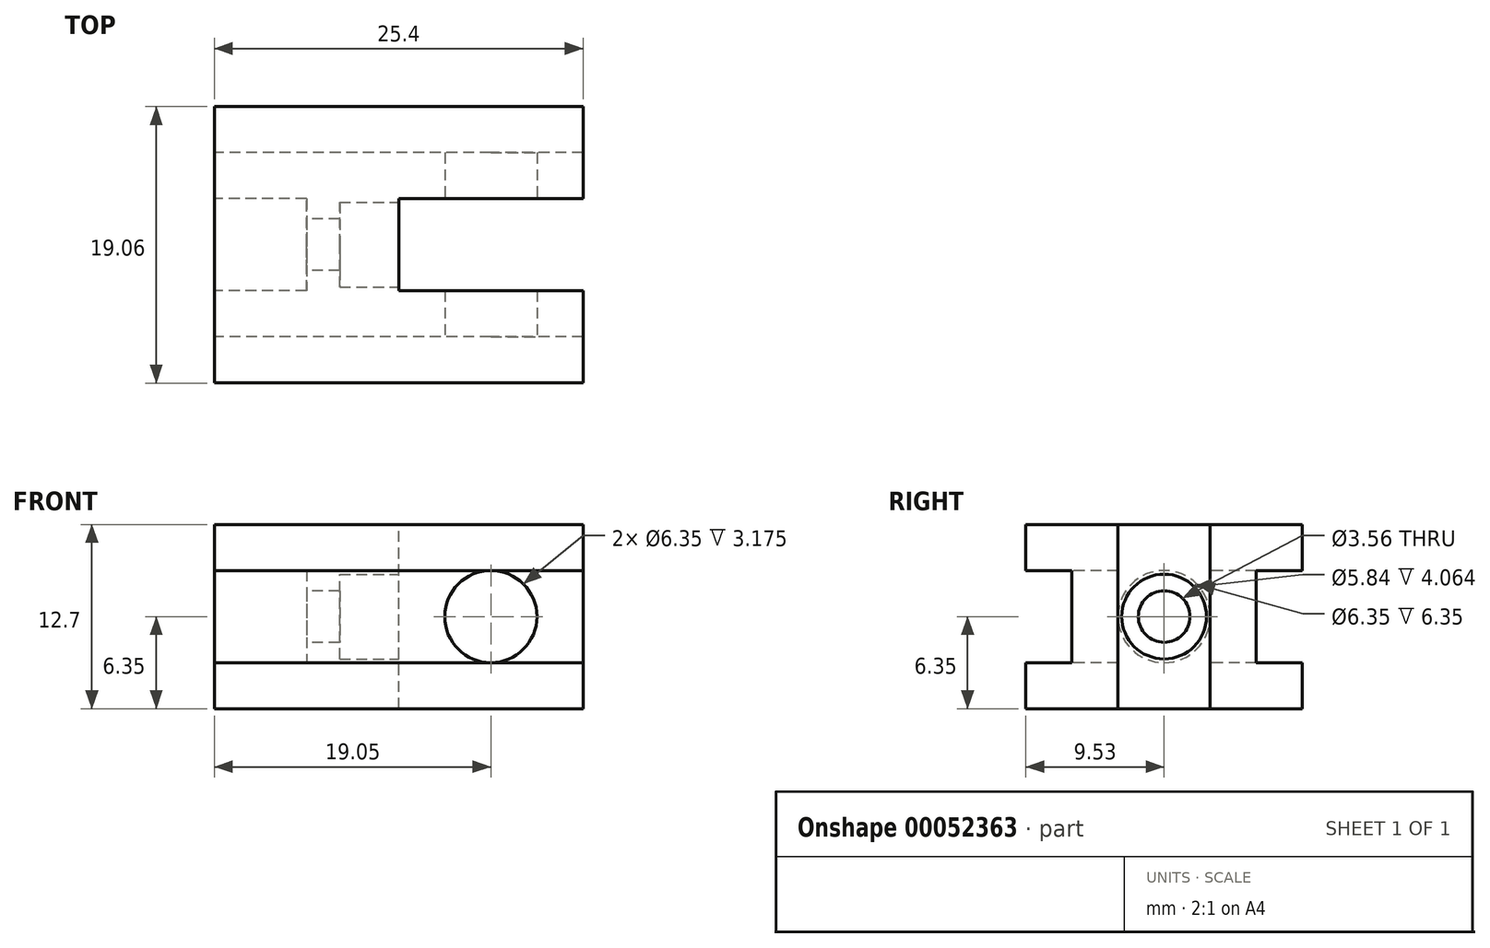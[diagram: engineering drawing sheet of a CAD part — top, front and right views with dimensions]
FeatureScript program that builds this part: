
annotation { "Feature Type Name" : "Feature", "Feature Type Description" : "" }
export const myFeature = defineFeature(function(context is Context, id is Id, definition is map)
    precondition{}
    {
        {
            var Q0;
            Q0=qCreatedBy(makeId("Right.planeOp"),FACE);
            var sketch = newSketch(context, id + "F0", { "sketchPlane" : qUnion([Q0])});
            skLineSegment(sketch, "E0", {"start": v(-6.35, -3.17) * mm, "end": v(-6.35, 3.17) * mm});
            skLineSegment(sketch, "E1", {"start": v(-6.35, 3.17) * mm, "end": v(-9.53, 3.17) * mm});
            skLineSegment(sketch, "E2", {"start": v(-9.52, 3.17) * mm, "end": v(-9.52, 6.35) * mm});
            skLineSegment(sketch, "E3", {"start": v(-9.52, 6.35) * mm, "end": v(9.52, 6.35) * mm});
            skLineSegment(sketch, "E4", {"start": v(9.53, 6.35) * mm, "end": v(9.53, 3.17) * mm});
            skLineSegment(sketch, "E5", {"start": v(9.53, 3.17) * mm, "end": v(6.35, 3.17) * mm});
            skLineSegment(sketch, "E6", {"start": v(6.35, 3.17) * mm, "end": v(6.35, -3.17) * mm});
            skLineSegment(sketch, "E7", {"start": v(6.35, -3.17) * mm, "end": v(9.53, -3.17) * mm});
            skLineSegment(sketch, "E8", {"start": v(9.52, -3.17) * mm, "end": v(9.52, -6.35) * mm});
            skLineSegment(sketch, "E9", {"start": v(9.53, -6.35) * mm, "end": v(-9.53, -6.35) * mm});
            skLineSegment(sketch, "E10", {"start": v(-9.53, -6.35) * mm, "end": v(-9.53, -3.17) * mm});
            skLineSegment(sketch, "E11", {"start": v(-9.53, -3.17) * mm, "end": v(-6.35, -3.17) * mm});
            skPoint(sketch, "E12", {"position": v(0, 6.35) * mm});
            skPoint(sketch, "E13", {"position": v(6.35, 0) * mm});
            skCircle(sketch, "E14", {"center": v(0, 0) * mm, "radius": 1.78 * mm});
            skSolve(sketch);
        }
        {
            var Q0;
            Q0 = qSketchRegion(id + "F0", true);
            extrude(context, id + "F1", {"entities" : qUnion([Q0]), "depth" : 25.4 * mm, "symmetric" : true});
        }
        {
            var Q0;
            Q0=qCreatedBy(makeId("Front.planeOp"),FACE);
            var sketch = newSketch(context, id + "F2", { "sketchPlane" : qUnion([Q0])});
            skCircle(sketch, "E15", {"center": v(6.35, 0) * mm, "radius": 3.18 * mm});
            skSolve(sketch);
        }
        {
            var Q0;
            Q0 = qSketchRegion(id + "F2", true);
            extrude(context, id + "F3", {"entities" : qUnion([Q0]), "operationType" : NewBodyOperationType.REMOVE, "oppositeDirection" : true, "depth" : 25.4 * mm, "symmetric" : true});
        }
        {
            var Q0;
            Q0=qCreatedBy(makeId("Top.planeOp"),FACE);
            var sketch = newSketch(context, id + "F4", { "sketchPlane" : qUnion([Q0])});
            skLineSegment(sketch, "E16.bottom", {"start": v(12.7, -3.18) * mm, "end": v(0, -3.18) * mm});
            skLineSegment(sketch, "E16.top", {"start": v(12.7, 3.18) * mm, "end": v(0, 3.18) * mm});
            skLineSegment(sketch, "E16.left", {"start": v(12.7, -3.18) * mm, "end": v(12.7, 3.18) * mm});
            skLineSegment(sketch, "E16.right", {"start": v(0, -3.18) * mm, "end": v(0, 3.18) * mm});
            skPoint(sketch, "E17", {"position": v(0, 0) * mm});
            skSolve(sketch);
        }
        {
            var Q0;
            Q0 = qSketchRegion(id + "F4", true);
            extrude(context, id + "F5", {"entities" : qUnion([Q0]), "operationType" : NewBodyOperationType.REMOVE, "oppositeDirection" : true, "depth" : 25.4 * mm, "symmetric" : true});
        }
        {
            var Q0;
            Q0=makeQuery(id+"F5.boolean.opBoolean","COPY",FACE,{"derivedFrom":makeQuery(id+"F5.opExtrude","SWEPT_FACE",FACE,{"disambiguationData":[OSD([sQuery(id+"F4.wireOp",EDGE,"E16.right")])]})});
            var sketch = newSketch(context, id + "F6", { "sketchPlane" : qUnion([Q0])});
            skCircle(sketch, "E18", {"center": v(0, 0) * mm, "radius": 2.92 * mm});
            skSolve(sketch);
        }
        {
            var Q0;
            Q0 = qSketchRegion(id + "F6", true);
            extrude(context, id + "F7", {"entities" : qUnion([Q0]), "operationType" : NewBodyOperationType.REMOVE, "oppositeDirection" : true, "depth" : 4.06 * mm});
        }
        {
            var Q0;
            Q0=makeQuery(id+"F1.opExtrude","CAP_FACE",FACE,{"disambiguationData":[OSD([sQuery(id+"F0.wireOp",EDGE,"E0"),sQuery(id+"F0.wireOp",EDGE,"E1"),sQuery(id+"F0.wireOp",EDGE,"E2"),sQuery(id+"F0.wireOp",EDGE,"E3"),sQuery(id+"F0.wireOp",EDGE,"E4"),sQuery(id+"F0.wireOp",EDGE,"E5"),sQuery(id+"F0.wireOp",EDGE,"E6"),sQuery(id+"F0.wireOp",EDGE,"E7"),sQuery(id+"F0.wireOp",EDGE,"E8"),sQuery(id+"F0.wireOp",EDGE,"E9"),sQuery(id+"F0.wireOp",EDGE,"E10"),sQuery(id+"F0.wireOp",EDGE,"E11"),sQuery(id+"F0.wireOp",EDGE,"E14")])],"isStart":true});
            var sketch = newSketch(context, id + "F8", { "sketchPlane" : qUnion([Q0])});
            skCircle(sketch, "E19", {"center": v(0, 0) * mm, "radius": 3.18 * mm});
            skSolve(sketch);
        }
        {
            var Q0;
            Q0 = qSketchRegion(id + "F8", true);
            extrude(context, id + "F9", {"entities" : qUnion([Q0]), "operationType" : NewBodyOperationType.REMOVE, "oppositeDirection" : true, "depth" : 6.35 * mm});
        }
    });
